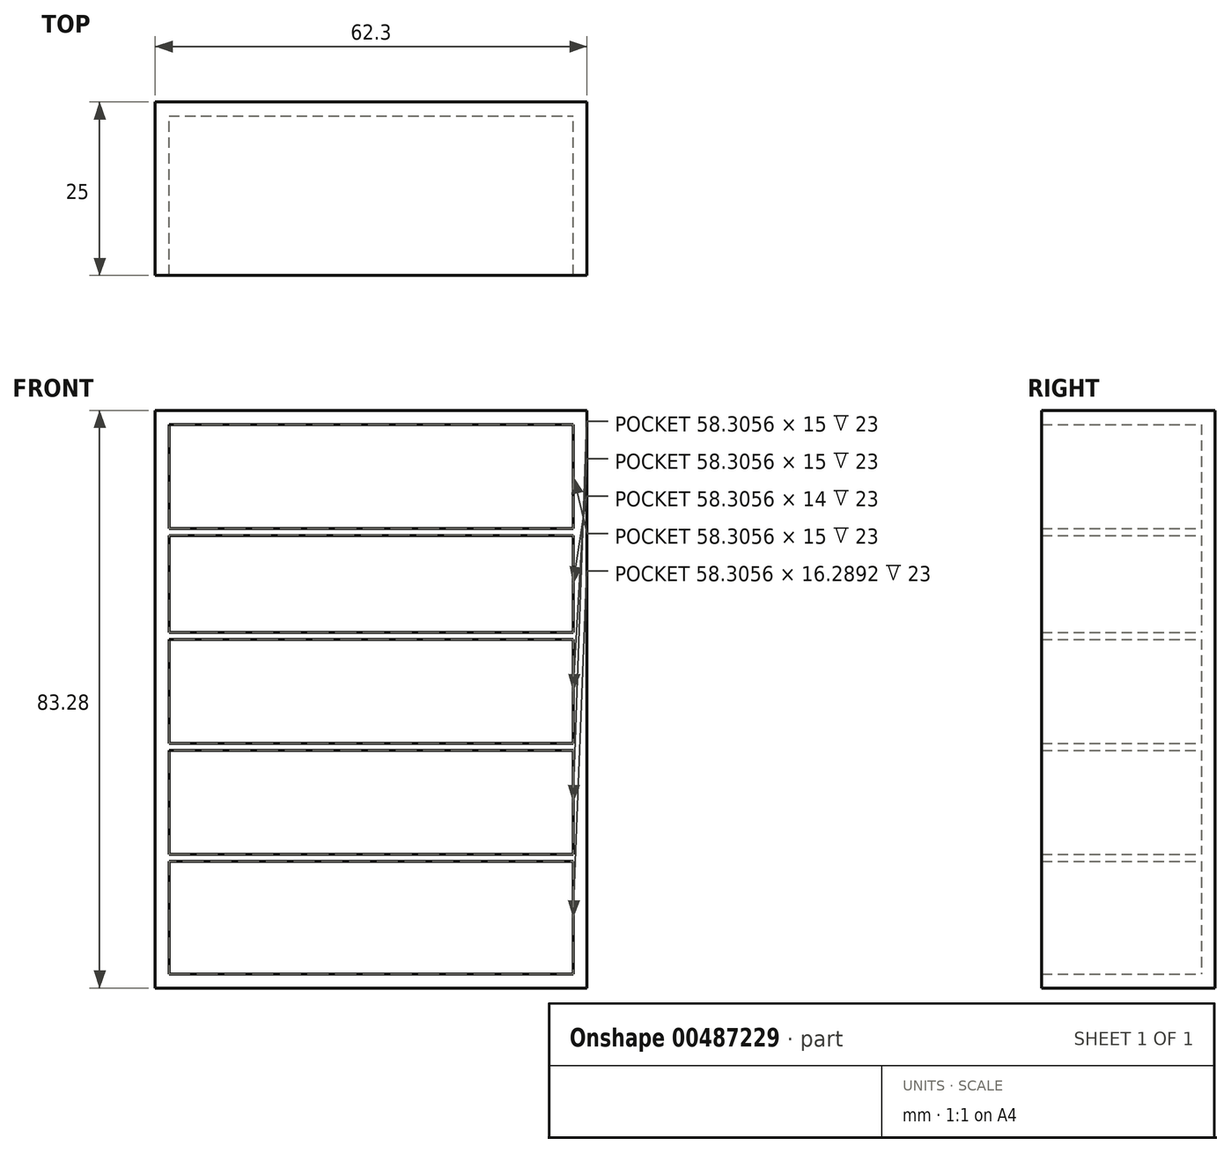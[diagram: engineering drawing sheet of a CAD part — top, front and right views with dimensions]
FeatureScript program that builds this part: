
annotation { "Feature Type Name" : "Feature", "Feature Type Description" : "" }
export const myFeature = defineFeature(function(context is Context, id is Id, definition is map)
    precondition{}
    {
        {
            var Q0;
            Q0=qCreatedBy(makeId("Front.planeOp"),FACE);
            var sketch = newSketch(context, id + "F0", { "sketchPlane" : qUnion([Q0])});
            skLineSegment(sketch, "E0.bottom", {"start": v(-31.15, 41.64) * mm, "end": v(31.15, 41.64) * mm});
            skLineSegment(sketch, "E0.top", {"start": v(-31.15, -41.64) * mm, "end": v(31.15, -41.64) * mm});
            skLineSegment(sketch, "E0.left", {"start": v(-31.15, 41.64) * mm, "end": v(-31.15, -41.64) * mm});
            skLineSegment(sketch, "E0.right", {"start": v(31.15, 41.64) * mm, "end": v(31.15, -41.64) * mm});
            skPoint(sketch, "E0.middle", {"position": v(0, 0) * mm});
            skLineSegment(sketch, "E1.0", {"start": v(-29.15, 39.64) * mm, "end": v(-29.15, -39.64) * mm});
            skLineSegment(sketch, "E1.1", {"start": v(-29.15, 39.64) * mm, "end": v(29.15, 39.64) * mm});
            skLineSegment(sketch, "E1.2", {"start": v(29.15, 39.64) * mm, "end": v(29.15, -39.64) * mm});
            skLineSegment(sketch, "E1.3", {"start": v(-29.15, -39.64) * mm, "end": v(29.15, -39.64) * mm});
            skSolve(sketch);
        }
        {
            var Q0;
            Q0 = qSketchRegion(id + "F0", true);
            extrude(context, id + "F1", {"entities" : qUnion([Q0]), "depth" : 25 * mm});
        }
        {
            var Q0;
            Q0=makeQuery(id+"F0.imprint","IMPRINT",FACE,{"disambiguationData":[TD([[makeQuery(id+"F0.imprint","IMPRINT",EDGE,{"derivedFrom":sQuery(id+"F0.wireOp",EDGE,"E1.0")}),1.0]])]});
            extrude(context, id + "F2", {"entities" : qUnion([Q0]), "operationType" : NewBodyOperationType.ADD, "depth" : 2 * mm});
        }
        {
            var Q0;
            Q0=makeQuery(id+"F2.opExtrude","CAP_FACE",FACE,{"disambiguationData":[OSD([sQuery(id+"F0.wireOp",EDGE,"E1.0"),sQuery(id+"F0.wireOp",EDGE,"E1.1"),sQuery(id+"F0.wireOp",EDGE,"E1.2"),sQuery(id+"F0.wireOp",EDGE,"E1.3")])],"isStart":false});
            var sketch = newSketch(context, id + "F3", { "sketchPlane" : qUnion([Q0])});
            skLineSegment(sketch, "E2", {"start": v(-29.15, 23.64) * mm, "end": v(29.15, 23.64) * mm});
            skLineSegment(sketch, "E3", {"start": v(-29.15, 9.64) * mm, "end": v(29.15, 9.64) * mm});
            skLineSegment(sketch, "E4", {"start": v(-29.15, -6.36) * mm, "end": v(29.15, -6.36) * mm});
            skLineSegment(sketch, "E5", {"start": v(-29.15, -22.36) * mm, "end": v(29.15, -22.36) * mm});
            skLineSegment(sketch, "E6.0", {"start": v(-29.15, 24.64) * mm, "end": v(29.15, 24.64) * mm});
            skLineSegment(sketch, "E7.0", {"start": v(-29.15, 8.64) * mm, "end": v(29.15, 8.64) * mm});
            skLineSegment(sketch, "E8.0", {"start": v(-29.15, -7.36) * mm, "end": v(29.15, -7.36) * mm});
            skLineSegment(sketch, "E9.0", {"start": v(-29.15, -23.36) * mm, "end": v(29.15, -23.36) * mm});
            skSolve(sketch);
        }
        {
            var Q0;
            {var subQ0=sQuery(id+"F3.wireOp",EDGE,"E2");Q0=makeQuery(id+"F3.imprint","IMPRINT",FACE,{"disambiguationData":[TD([[makeQuery(id+"F3.imprint","IMPRINT",EDGE,{"derivedFrom":subQ0}),1.0]])]});}
            var Q1;
            {var subQ0=sQuery(id+"F3.wireOp",EDGE,"E3");Q1=makeQuery(id+"F3.imprint","IMPRINT",FACE,{"disambiguationData":[TD([[makeQuery(id+"F3.imprint","IMPRINT",EDGE,{"derivedFrom":subQ0}),-1.0]])]});}
            var Q2;
            {var subQ0=sQuery(id+"F3.wireOp",EDGE,"E4");Q2=makeQuery(id+"F3.imprint","IMPRINT",FACE,{"disambiguationData":[TD([[makeQuery(id+"F3.imprint","IMPRINT",EDGE,{"derivedFrom":subQ0}),-1.0]])]});}
            var Q3;
            {var subQ0=sQuery(id+"F3.wireOp",EDGE,"E5");Q3=makeQuery(id+"F3.imprint","IMPRINT",FACE,{"disambiguationData":[TD([[makeQuery(id+"F3.imprint","IMPRINT",EDGE,{"derivedFrom":subQ0}),-1.0]])]});}
            extrude(context, id + "F4", {"entities" : qUnion([Q0, Q1, Q2, Q3]), "operationType" : NewBodyOperationType.ADD, "depth" : 23 * mm});
        }
    });
